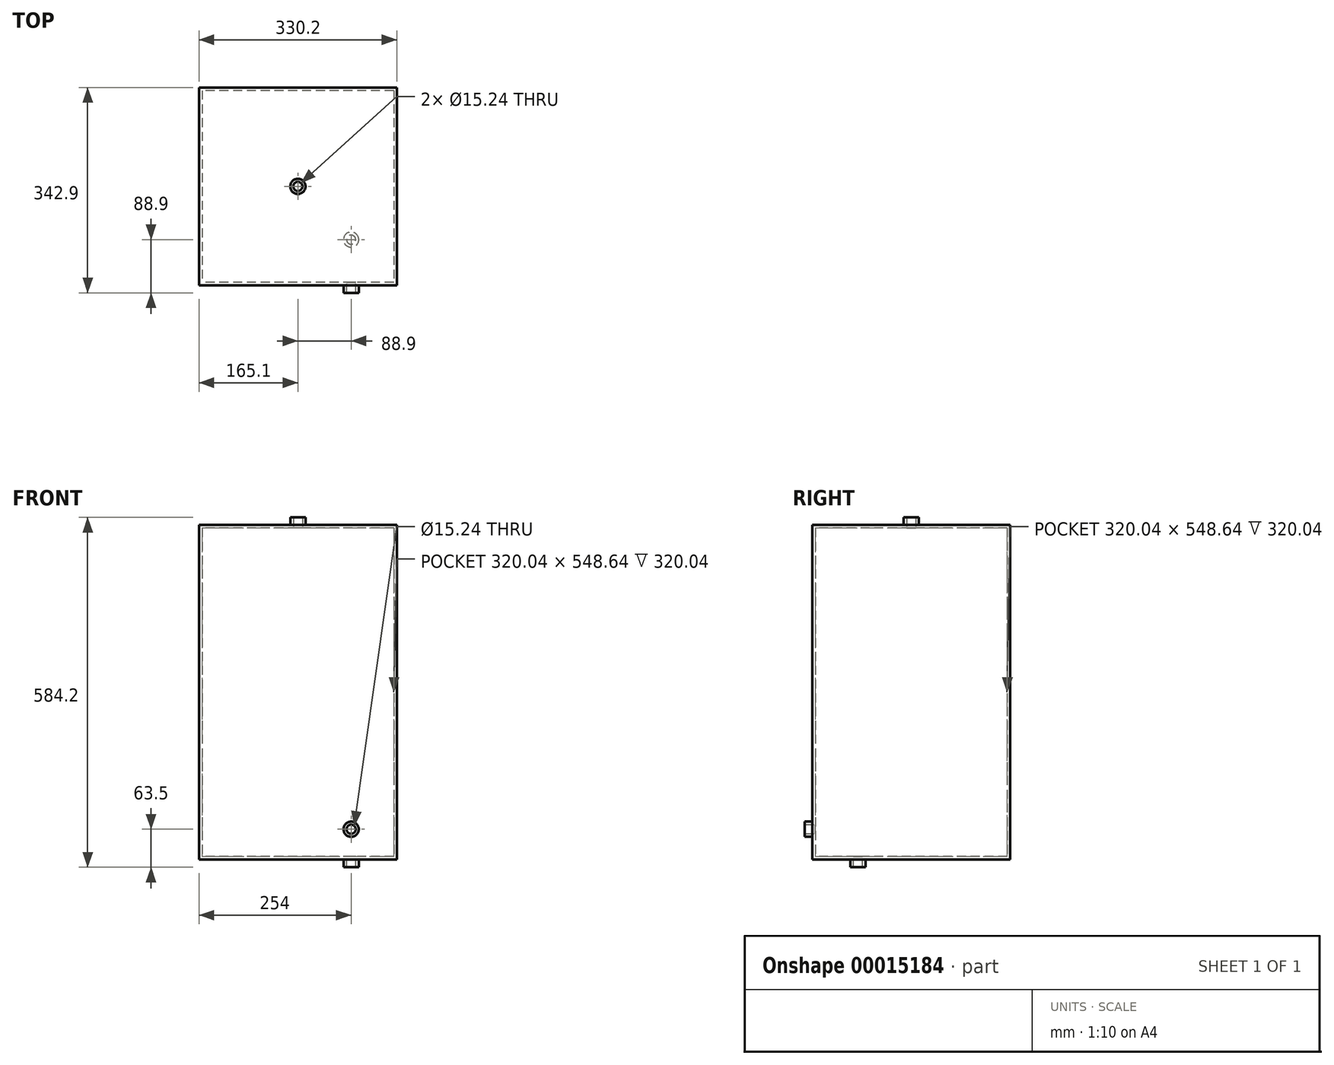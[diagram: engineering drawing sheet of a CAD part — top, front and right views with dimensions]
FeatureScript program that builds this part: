
annotation { "Feature Type Name" : "Feature", "Feature Type Description" : "" }
export const myFeature = defineFeature(function(context is Context, id is Id, definition is map)
    precondition{}
    {
        {
            var Q0;
            Q0=qCreatedBy(makeId("Top.planeOp"),FACE);
            var sketch = newSketch(context, id + "F0", { "sketchPlane" : qUnion([Q0])});
            skLineSegment(sketch, "E0.rect.bottom", {"start": v(165.1, 165.1) * mm, "end": v(-165.1, 165.1) * mm});
            skLineSegment(sketch, "E0.rect.top", {"start": v(165.1, -165.1) * mm, "end": v(-165.1, -165.1) * mm});
            skLineSegment(sketch, "E0.rect.left", {"start": v(165.1, 165.1) * mm, "end": v(165.1, -165.1) * mm});
            skLineSegment(sketch, "E0.rect.right", {"start": v(-165.1, 165.1) * mm, "end": v(-165.1, -165.1) * mm});
            skPoint(sketch, "E0.rect.middle", {"position": v(0, 0) * mm});
            skSolve(sketch);
        }
        {
            var Q0;
            Q0=makeQuery(id+"F0.imprint","IMPRINT",FACE,{"disambiguationData":[TD([[makeQuery(id+"F0.imprint","IMPRINT",EDGE,{"derivedFrom":sQuery(id+"F0.wireOp",EDGE,"E0.rect.bottom")}),1.0]])]});
            extrude(context, id + "F1", {"entities" : qUnion([Q0]), "depth" : 558.8 * mm});
        }
        {
            var Q0;
            Q0=makeQuery(id+"F1.opExtrude","CAP_FACE",FACE,{"disambiguationData":[OSD([sQuery(id+"F0.wireOp",EDGE,"E0.rect.bottom"),sQuery(id+"F0.wireOp",EDGE,"E0.rect.top"),sQuery(id+"F0.wireOp",EDGE,"E0.rect.left"),sQuery(id+"F0.wireOp",EDGE,"E0.rect.right")])],"isStart":false});
            var sketch = newSketch(context, id + "F2", { "sketchPlane" : qUnion([Q0])});
            skCircle(sketch, "E1", {"center": v(0, 0) * mm, "radius": 12.7 * mm});
            skSolve(sketch);
        }
        {
            var Q0;
            Q0=makeQuery(id+"F2.imprint","IMPRINT",FACE,{"disambiguationData":[TD([[makeQuery(id+"F2.imprint","IMPRINT",EDGE,{"derivedFrom":sQuery(id+"F2.wireOp",EDGE,"E1")}),1.0]])]});
            extrude(context, id + "F3", {"entities" : qUnion([Q0]), "operationType" : NewBodyOperationType.ADD, "depth" : 12.7 * mm});
        }
        {
            var Q0;
            Q0=makeQuery(id+"F1.opExtrude","SWEPT_FACE",FACE,{"disambiguationData":[OSD([sQuery(id+"F0.wireOp",EDGE,"E0.rect.top")])]});
            var sketch = newSketch(context, id + "F4", { "sketchPlane" : qUnion([Q0])});
            skCircle(sketch, "E2", {"center": v(88.9, 50.8) * mm, "radius": 12.7 * mm});
            skSolve(sketch);
        }
        {
            var Q0;
            Q0=makeQuery(id+"F4.imprint","IMPRINT",FACE,{"disambiguationData":[TD([[makeQuery(id+"F4.imprint","IMPRINT",EDGE,{"derivedFrom":sQuery(id+"F4.wireOp",EDGE,"E2")}),1.0]])]});
            extrude(context, id + "F5", {"entities" : qUnion([Q0]), "operationType" : NewBodyOperationType.ADD, "depth" : 12.7 * mm});
        }
        {
            var Q0;
            Q0=makeQuery(id+"F1.opExtrude","CAP_FACE",FACE,{"disambiguationData":[OSD([sQuery(id+"F0.wireOp",EDGE,"E0.rect.bottom"),sQuery(id+"F0.wireOp",EDGE,"E0.rect.top"),sQuery(id+"F0.wireOp",EDGE,"E0.rect.left"),sQuery(id+"F0.wireOp",EDGE,"E0.rect.right")])],"isStart":true});
            var sketch = newSketch(context, id + "F6", { "sketchPlane" : qUnion([Q0])});
            skCircle(sketch, "E3", {"center": v(88.9, 88.9) * mm, "radius": 12.7 * mm});
            skSolve(sketch);
        }
        {
            var Q0;
            Q0=makeQuery(id+"F6.imprint","IMPRINT",FACE,{"disambiguationData":[TD([[makeQuery(id+"F6.imprint","IMPRINT",EDGE,{"derivedFrom":sQuery(id+"F6.wireOp",EDGE,"E3")}),1.0]])]});
            extrude(context, id + "F7", {"entities" : qUnion([Q0]), "operationType" : NewBodyOperationType.ADD, "depth" : 12.7 * mm});
        }
        {
            var Q0;
            Q0=makeQuery(id+"F3.opExtrude","CAP_FACE",FACE,{"disambiguationData":[OSD([sQuery(id+"F2.wireOp",EDGE,"E1")])],"isStart":false});
            var Q1;
            Q1=makeQuery(id+"F5.opExtrude","CAP_FACE",FACE,{"disambiguationData":[OSD([sQuery(id+"F4.wireOp",EDGE,"E2")])],"isStart":false});
            var Q2;
            Q2=makeQuery(id+"F7.opExtrude","CAP_FACE",FACE,{"disambiguationData":[OSD([sQuery(id+"F6.wireOp",EDGE,"E3")])],"isStart":false});
            shell(context, id + "F8", {"entities" : qUnion([Q0, Q1, Q2]), "thickness" : 5.08 * mm});
        }
    });
